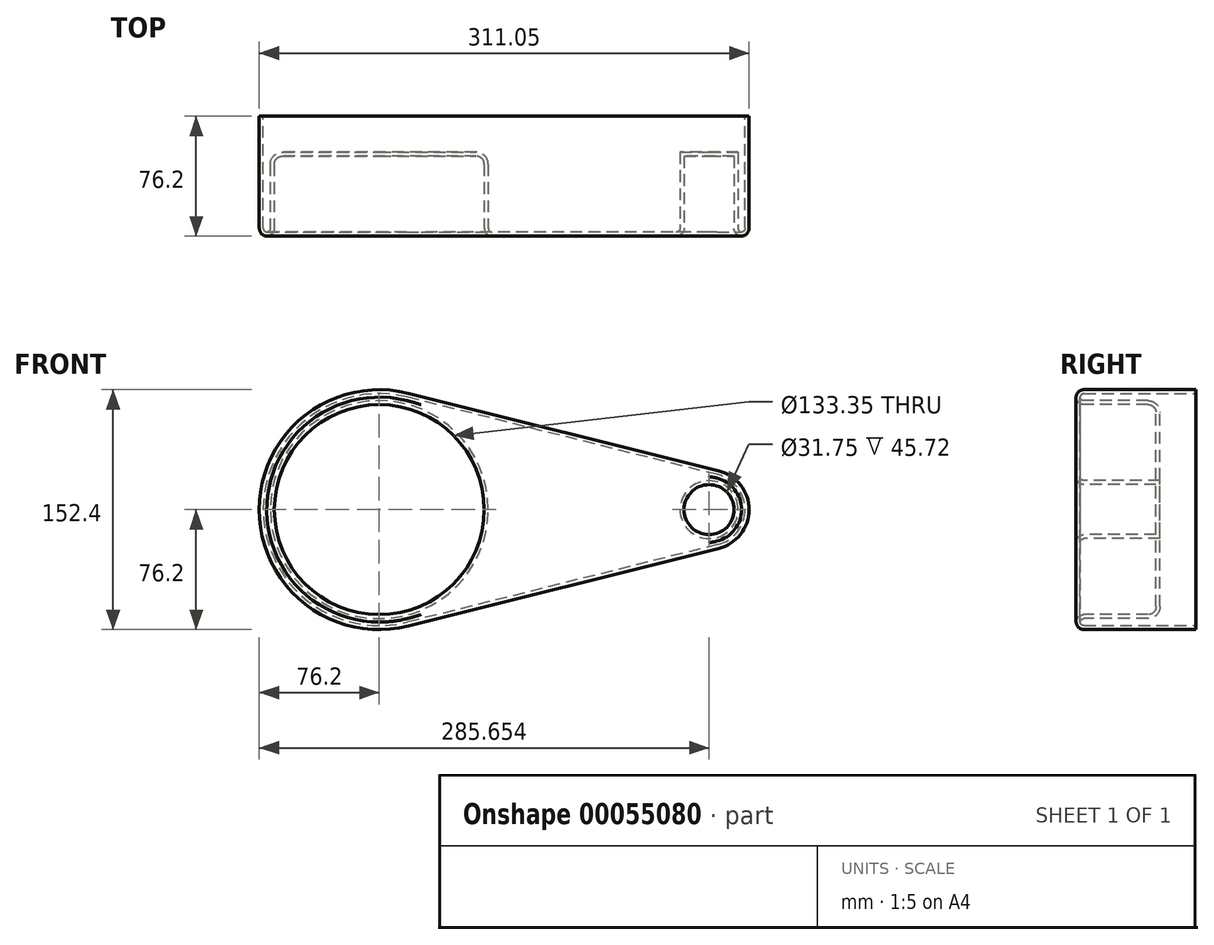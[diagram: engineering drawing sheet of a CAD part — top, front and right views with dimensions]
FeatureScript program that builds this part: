
annotation { "Feature Type Name" : "Feature", "Feature Type Description" : "" }
export const myFeature = defineFeature(function(context is Context, id is Id, definition is map)
    precondition{}
    {
        {
            var Q0;
            Q0=qCreatedBy(makeId("Front.planeOp"),FACE);
            var sketch = newSketch(context, id + "F0", { "sketchPlane" : qUnion([Q0])});
            skCircle(sketch, "E0", {"center": v(0, 0) * mm, "radius": 76.2 * mm});
            skCircle(sketch, "E1", {"center": v(209.45, 0) * mm, "radius": 25.4 * mm});
            skLineSegment(sketch, "E2", {"start": v(215.61, 24.64) * mm, "end": v(18.48, 73.92) * mm});
            skLineSegment(sketch, "E3", {"start": v(215.61, -24.64) * mm, "end": v(18.48, -73.92) * mm});
            skSolve(sketch);
        }
        {
            var Q0;
            Q0 = qSketchRegion(id + "F0", true);
            extrude(context, id + "F1", {"entities" : qUnion([Q0]), "depth" : 76.2 * mm});
        }
        {
            var Q0;
            Q0=makeQuery(id+"F1.opExtrude","CAP_FACE",FACE,{"disambiguationData":[OSD([sQuery(id+"F0.wireOp",EDGE,"E0"),sQuery(id+"F0.wireOp",EDGE,"E1"),sQuery(id+"F0.wireOp",EDGE,"E2"),sQuery(id+"F0.wireOp",EDGE,"E3")])],"isStart":false});
            var sketch = newSketch(context, id + "F2", { "sketchPlane" : qUnion([Q0])});
            skCircle(sketch, "E4", {"center": v(0, 0) * mm, "radius": 66.68 * mm});
            skCircle(sketch, "E5", {"center": v(209.45, 0) * mm, "radius": 15.88 * mm});
            skSolve(sketch);
        }
        {
            var Q0;
            Q0=makeQuery(id+"F2.imprint","IMPRINT",FACE,{"disambiguationData":[TD([[makeQuery(id+"F2.imprint","IMPRINT",EDGE,{"derivedFrom":sQuery(id+"F2.wireOp",EDGE,"E5")}),1.0]])]});
            var Q1;
            Q1=makeQuery(id+"F2.imprint","IMPRINT",FACE,{"disambiguationData":[TD([[makeQuery(id+"F2.imprint","IMPRINT",EDGE,{"derivedFrom":sQuery(id+"F2.wireOp",EDGE,"E4")}),1.0]])]});
            extrude(context, id + "F3", {"entities" : qUnion([Q0, Q1]), "operationType" : NewBodyOperationType.REMOVE, "oppositeDirection" : true, "depth" : 50.8 * mm});
        }
        {
            var Q0;
            Q0=makeQuery(id+"F1.opExtrude","CAP_FACE",FACE,{"disambiguationData":[OSD([sQuery(id+"F0.wireOp",EDGE,"E0"),sQuery(id+"F0.wireOp",EDGE,"E1"),sQuery(id+"F0.wireOp",EDGE,"E2"),sQuery(id+"F0.wireOp",EDGE,"E3")])],"isStart":false});
            var Q1;
            Q1=makeQuery(id+"F3.boolean.opBoolean","COPY",EDGE,{"derivedFrom":makeQuery(id+"F3.opExtrude","CAP_EDGE",EDGE,{"disambiguationData":[OSD([sQuery(id+"F2.wireOp",EDGE,"E4")])],"isStart":false})});
            fillet(context, id + "F4", {"entities" : qUnion([Q0, Q1]), "radius" : 5.08 * mm, "tangentPropagation" : true, "allowEdgeOverflow" : false});
        }
        {
            var Q0;
            Q0=makeQuery(id+"F1.opExtrude","CAP_FACE",FACE,{"disambiguationData":[OSD([sQuery(id+"F0.wireOp",EDGE,"E0"),sQuery(id+"F0.wireOp",EDGE,"E1"),sQuery(id+"F0.wireOp",EDGE,"E2"),sQuery(id+"F0.wireOp",EDGE,"E3")])],"isStart":true});
            shell(context, id + "F5", {"entities" : qUnion([Q0]), "thickness" : 2.54 * mm});
        }
    });
